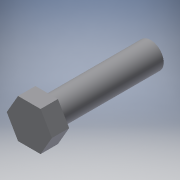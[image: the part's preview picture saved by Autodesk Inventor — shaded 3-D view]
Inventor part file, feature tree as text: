
AUTODESK INVENTOR PART (.ipt)
format: ipt  version: 2016 (Build 200138000, 138)  size: 99,328 bytes
history: native  units: in
note: dims shown in document units (in); Inventor stores cm internally (conversion verified against a paired STEP export)
features: extrude x2, sketch x2
ambient origin geometry x8: Origin, YZ Plane, XZ Plane, XY Plane, X Axis, Y Axis, Z Axis, Center Point
bodies: Solid1 (feature_tree)
feature tree (4):
  extrude  "Extrusion1"  Depth=0.25in TaperAngle=0.0deg
  extrude  "Extrusion2"  Depth=1.5in TaperAngle=0.0deg
  sketch  "Sketch1"  dims[d0=0.5625in d1=0.25in d2=0.0in]
  sketch  "Sketch2"  dims[d3=0.375in d4=1.5in d5=0.0in]
